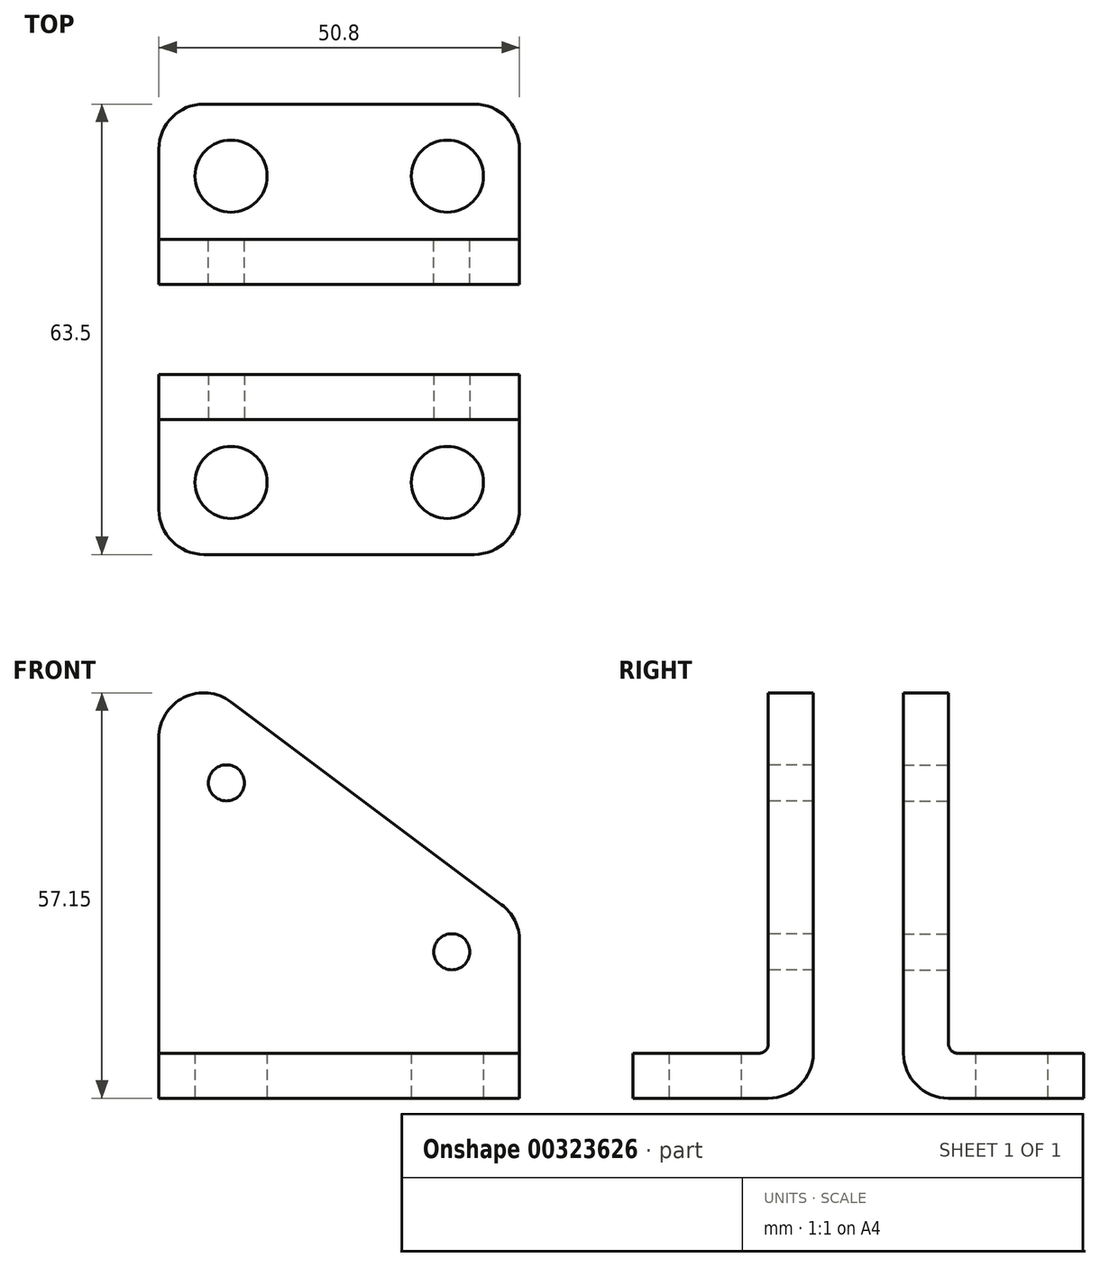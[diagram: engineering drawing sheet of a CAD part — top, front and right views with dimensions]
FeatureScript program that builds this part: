
annotation { "Feature Type Name" : "Feature", "Feature Type Description" : "" }
export const myFeature = defineFeature(function(context is Context, id is Id, definition is map)
    precondition{}
    {
        {
            var Q0;
            Q0=qCreatedBy(makeId("Top.planeOp"),FACE);
            var sketch = newSketch(context, id + "F0", { "sketchPlane" : qUnion([Q0])});
            skLineSegment(sketch, "E0.bottom", {"start": v(-25.4, 31.75) * mm, "end": v(25.4, 31.75) * mm});
            skLineSegment(sketch, "E0.top", {"start": v(-25.4, 6.35) * mm, "end": v(25.4, 6.35) * mm});
            skLineSegment(sketch, "E0.left", {"start": v(-25.4, 31.75) * mm, "end": v(-25.4, 6.35) * mm});
            skLineSegment(sketch, "E0.right", {"start": v(25.4, 31.75) * mm, "end": v(25.4, 6.35) * mm});
            skPoint(sketch, "E1", {"position": v(0, 31.75) * mm});
            skLineSegment(sketch, "E2.0", {"start": v(-25.4, 12.7) * mm, "end": v(25.4, 12.7) * mm});
            skCircle(sketch, "E3", {"center": v(15.24, 21.59) * mm, "radius": 5.08 * mm});
            skCircle(sketch, "E4", {"center": v(-15.24, 21.59) * mm, "radius": 5.08 * mm});
            skSolve(sketch);
        }
        {
            var Q0;
            Q0 = qSketchRegion(id + "F0", true);
            extrude(context, id + "F1", {"entities" : qUnion([Q0]), "depth" : 6.35 * mm});
        }
        {
            var Q0;
            {var subQ0=sQuery(id+"F0.wireOp",EDGE,"E0.top");Q0=makeQuery(id+"F0.imprint","IMPRINT",FACE,{"disambiguationData":[TD([[makeQuery(id+"F0.imprint","IMPRINT",EDGE,{"derivedFrom":subQ0}),1.0]])]});}
            extrude(context, id + "F2", {"entities" : qUnion([Q0]), "operationType" : NewBodyOperationType.ADD, "depth" : 63.5 * mm});
        }
        {
            var Q0;
            Q0=makeQuery(id+"F2.opExtrude","CAP_EDGE",EDGE,{"disambiguationData":[OSD([sQuery(id+"F0.wireOp",EDGE,"E0.right")])],"isStart":false});
            chamfer(context, id + "F3", {"entities" : qUnion([Q0]), "chamferType" : ChamferType.TWO_OFFSETS, "width1" : 50.8 * mm, "oppositeDirection" : true, "width2" : 38.1 * mm, "tangentPropagation" : true});
        }
        {
            var Q0;
            {var subQ0=sQuery(id+"F0.wireOp",EDGE,"E0.right");Q0=makeQuery(id+"F3.opChamfer","BLEND_EDGE",EDGE,{"blendedFrom":[makeQuery(id+"F2.opExtrude","CAP_EDGE",EDGE,{"disambiguationData":[OSD([subQ0])],"isStart":false}),makeQuery(id+"F2.boolean.opBoolean","MERGE",FACE,{"derivedFrom":[makeQuery(id+"F1.opExtrude","SWEPT_FACE",FACE,{"disambiguationData":[OSD([subQ0])]}),makeQuery(id+"F2.opExtrude","SWEPT_FACE",FACE,{"disambiguationData":[OSD([subQ0])]})]})],"blendedInto":[makeQuery(id+"F2.boolean.opBoolean","MERGE",FACE,{"derivedFrom":[makeQuery(id+"F1.opExtrude","SWEPT_FACE",FACE,{"disambiguationData":[OSD([subQ0])]}),makeQuery(id+"F2.opExtrude","SWEPT_FACE",FACE,{"disambiguationData":[OSD([subQ0])]})]})]});}
            var Q1;
            {var subQ0=sQuery(id+"F0.wireOp",EDGE,"E0.left");Q1=makeQuery(id+"F3.opChamfer","BLEND_EDGE",EDGE,{"blendedFrom":[makeQuery(id+"F2.opExtrude","CAP_EDGE",EDGE,{"disambiguationData":[OSD([sQuery(id+"F0.wireOp",EDGE,"E0.right")])],"isStart":false}),makeQuery(id+"F2.boolean.opBoolean","MERGE",FACE,{"derivedFrom":[makeQuery(id+"F1.opExtrude","SWEPT_FACE",FACE,{"disambiguationData":[OSD([subQ0])]}),makeQuery(id+"F2.opExtrude","SWEPT_FACE",FACE,{"disambiguationData":[OSD([subQ0])]})]})],"blendedInto":[makeQuery(id+"F2.boolean.opBoolean","MERGE",FACE,{"derivedFrom":[makeQuery(id+"F1.opExtrude","SWEPT_FACE",FACE,{"disambiguationData":[OSD([subQ0])]}),makeQuery(id+"F2.opExtrude","SWEPT_FACE",FACE,{"disambiguationData":[OSD([subQ0])]})]})]});}
            var Q2;
            Q2=makeQuery(id+"F1.opExtrude","SWEPT_EDGE",EDGE,{"disambiguationData":[OSD([sQuery(id+"F0.wireOp",EDGE,"E0.bottom"),sQuery(id+"F0.wireOp",EDGE,"E0.right")])]});
            var Q3;
            Q3=makeQuery(id+"F1.opExtrude","SWEPT_EDGE",EDGE,{"disambiguationData":[OSD([sQuery(id+"F0.wireOp",EDGE,"E0.bottom"),sQuery(id+"F0.wireOp",EDGE,"E0.left")])]});
            var Q4;
            Q4=makeQuery(id+"F1.opExtrude","CAP_EDGE",EDGE,{"disambiguationData":[OSD([sQuery(id+"F0.wireOp",EDGE,"E0.top")])],"isStart":true});
            fillet(context, id + "F4", {"entities" : qUnion([Q0, Q1, Q2, Q3, Q4]), "radius" : 6.35 * mm, "tangentPropagation" : true, "allowEdgeOverflow" : false});
        }
        {
            var Q0;
            Q0=makeQuery(id+"F2.boolean.opBoolean","INTERSECT",EDGE,{"derivedFrom":[makeQuery(id+"F1.opExtrude","CAP_FACE",FACE,{"disambiguationData":[OSD([sQuery(id+"F0.wireOp",EDGE,"E0.bottom"),sQuery(id+"F0.wireOp",EDGE,"E0.top"),sQuery(id+"F0.wireOp",EDGE,"E0.left"),sQuery(id+"F0.wireOp",EDGE,"E0.right"),sQuery(id+"F0.wireOp",EDGE,"E3"),sQuery(id+"F0.wireOp",EDGE,"E4")])],"isStart":false}),makeQuery(id+"F2.opExtrude","SWEPT_FACE",FACE,{"disambiguationData":[OSD([sQuery(id+"F0.wireOp",EDGE,"E2.0")])]})]});
            fillet(context, id + "F5", {"entities" : qUnion([Q0]), "radius" : 1.27 * mm, "tangentPropagation" : true, "allowEdgeOverflow" : false});
        }
        {
            var Q0;
            Q0=makeQuery(id+"F2.opExtrude","SWEPT_FACE",FACE,{"disambiguationData":[OSD([sQuery(id+"F0.wireOp",EDGE,"E2.0")])]});
            var sketch = newSketch(context, id + "F6", { "sketchPlane" : qUnion([Q0])});
            skPoint(sketch, "E5", {"position": v(15.88, 44.45) * mm});
            skPoint(sketch, "E6", {"position": v(-15.88, 20.64) * mm});
            skCircle(sketch, "E7", {"center": v(-15.88, 20.64) * mm, "radius": 2.54 * mm});
            skCircle(sketch, "E8", {"center": v(15.88, 44.45) * mm, "radius": 2.54 * mm});
            skSolve(sketch);
        }
        {
            var Q0;
            Q0 = qSketchRegion(id + "F6", true);
            extrude(context, id + "F7", {"entities" : qUnion([Q0]), "operationType" : NewBodyOperationType.REMOVE, "oppositeDirection" : true, "depth" : 25.4 * mm});
        }
        {
            var Q0;
            Q0=makeQuery(id+"F1.opExtrude","SWEPT_BODY",BODY,{"disambiguationData":[OSD([sQuery(id+"F0.wireOp",EDGE,"E0.bottom"),sQuery(id+"F0.wireOp",EDGE,"E0.top"),sQuery(id+"F0.wireOp",EDGE,"E0.left"),sQuery(id+"F0.wireOp",EDGE,"E0.right"),sQuery(id+"F0.wireOp",EDGE,"E3"),sQuery(id+"F0.wireOp",EDGE,"E4")])]});
            var Q1;
            Q1=qCreatedBy(makeId("Front.planeOp"),FACE);
            mirror(context, id + "F8", {"entities" : qUnion([Q0]), "mirrorPlane" : qUnion([Q1])});
        }
    });
